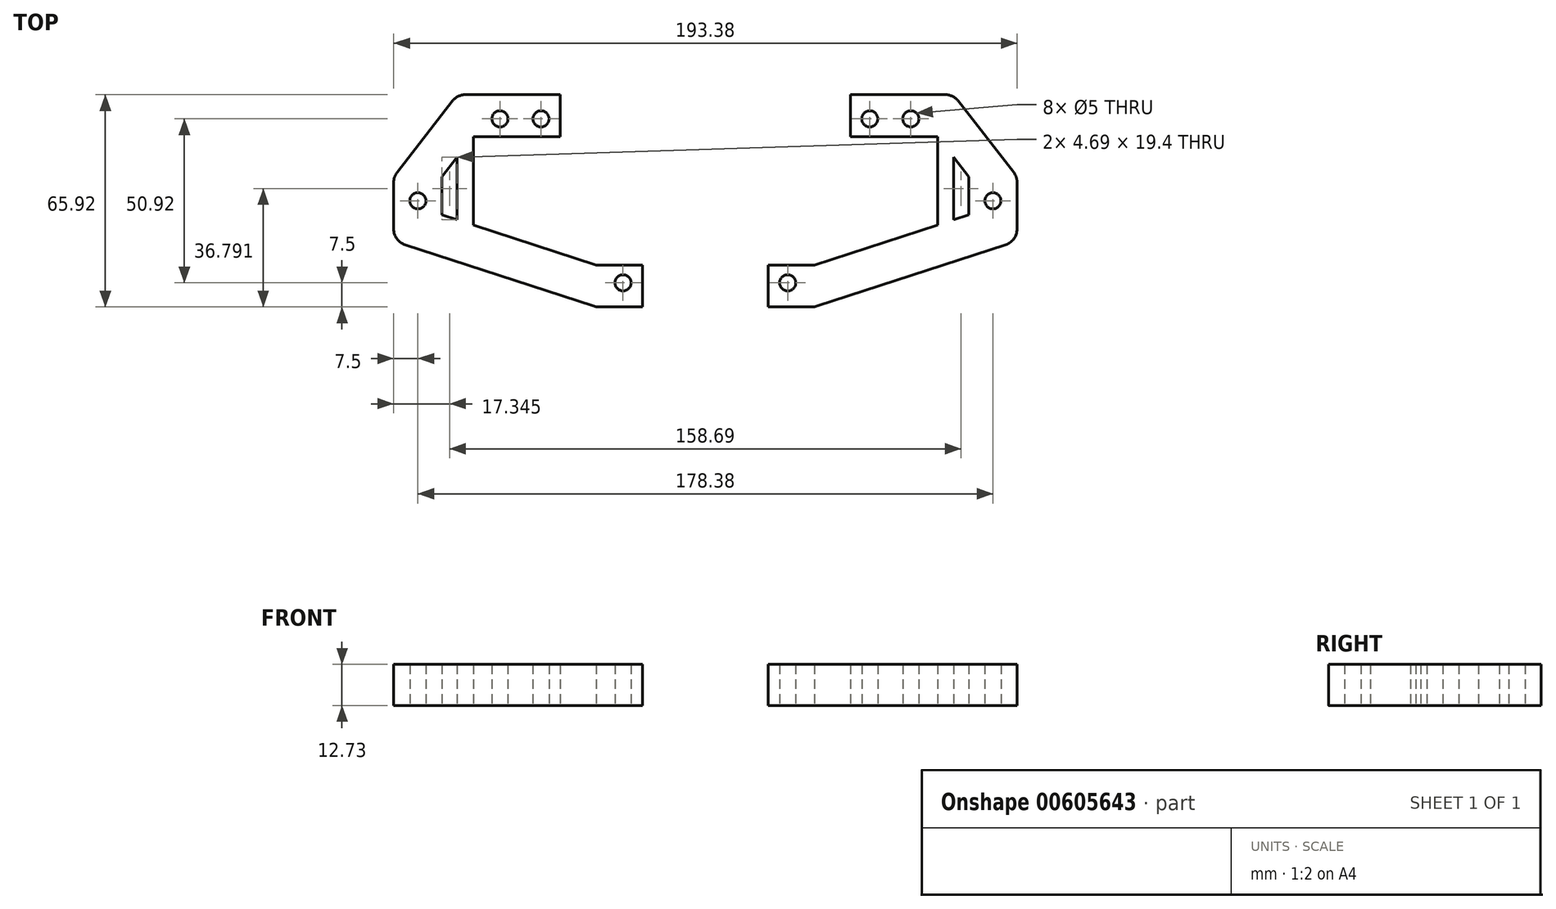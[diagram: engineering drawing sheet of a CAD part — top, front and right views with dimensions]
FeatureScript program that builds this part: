
annotation { "Feature Type Name" : "Feature", "Feature Type Description" : "" }
export const myFeature = defineFeature(function(context is Context, id is Id, definition is map)
    precondition{}
    {
        {
            var Q0;
            Q0=qCreatedBy(makeId("Top.planeOp"),FACE);
            var sketch = newSketch(context, id + "F0", { "sketchPlane" : qUnion([Q0])});
            skPoint(sketch, "E0", {"position": v(0, 0) * mm});
            skPoint(sketch, "E1", {"position": v(0, -50.92) * mm});
            skPoint(sketch, "E2", {"position": v(25.46, -50.92) * mm});
            skPoint(sketch, "E3", {"position": v(-12.73, 0) * mm});
            skPoint(sketch, "E4", {"position": v(0, -25.46) * mm});
            skPoint(sketch, "E5", {"position": v(-38.2, -25.46) * mm});
            skLineSegment(sketch, "E6.left", {"start": v(-45.7, -32.96) * mm, "end": v(-45.7, -17.96) * mm});
            skPoint(sketch, "E7.start.orphan", {"position": v(6, 0) * mm});
            skLineSegment(sketch, "E8", {"start": v(6, 5.5) * mm, "end": v(6, -5.5) * mm});
            skLineSegment(sketch, "E9", {"start": v(6, -5.5) * mm, "end": v(-21, -5.5) * mm});
            skLineSegment(sketch, "E10", {"start": v(31.46, -45.42) * mm, "end": v(17.2, -45.42) * mm});
            skLineSegment(sketch, "E11", {"start": v(-45.69, -17.96) * mm, "end": v(-27.45, 5.5) * mm});
            skLineSegment(sketch, "E12", {"start": v(-21, -5.5) * mm, "end": v(-21, -32.96) * mm});
            skLineSegment(sketch, "E13", {"start": v(-21, -32.96) * mm, "end": v(17.2, -45.42) * mm});
            skLineSegment(sketch, "E14", {"start": v(-45.7, -35.9) * mm, "end": v(-45.7, -32.96) * mm});
            skCircle(sketch, "E15", {"center": v(-12.73, 0) * mm, "radius": 2.5 * mm});
            skCircle(sketch, "E16", {"center": v(0, 0) * mm, "radius": 2.5 * mm});
            skCircle(sketch, "E17", {"center": v(-38.2, -25.46) * mm, "radius": 2.5 * mm});
            skCircle(sketch, "E18", {"center": v(25.46, -50.92) * mm, "radius": 2.5 * mm});
            skPoint(sketch, "E19", {"position": v(-30.7, -25.46) * mm});
            skLineSegment(sketch, "E20", {"start": v(-21, -32.96) * mm, "end": v(-30.7, -29.8) * mm});
            skLineSegment(sketch, "E21", {"start": v(-21, -5.5) * mm, "end": v(-30.7, -17.96) * mm});
            skLineSegment(sketch, "E22", {"start": v(-30.7, -17.96) * mm, "end": v(-30.7, -29.8) * mm});
            skPoint(sketch, "E23", {"position": v(-26, -25.46) * mm});
            skLineSegment(sketch, "E24", {"start": v(-26, -25.46) * mm, "end": v(-26, -11.93) * mm});
            skLineSegment(sketch, "E25", {"start": v(-26, -25.46) * mm, "end": v(-26, -31.33) * mm});
            skPoint(sketch, "E26", {"position": v(6, 7.5) * mm});
            skLineSegment(sketch, "E27", {"start": v(6, 7.5) * mm, "end": v(-25.9, 7.5) * mm});
            skLineSegment(sketch, "E28", {"start": v(-27.45, 5.5) * mm, "end": v(-25.9, 7.5) * mm});
            skLineSegment(sketch, "E29", {"start": v(6, 7.5) * mm, "end": v(6, 5.5) * mm});
            skLineSegment(sketch, "E30", {"start": v(17.2, -58.42) * mm, "end": v(-45.7, -37.9) * mm});
            skLineSegment(sketch, "E31", {"start": v(-45.7, -37.9) * mm, "end": v(-45.7, -35.9) * mm});
            skLineSegment(sketch, "E32", {"start": v(17.2, -58.42) * mm, "end": v(31.46, -58.42) * mm});
            skPoint(sketch, "E33", {"position": v(31.46, -50.92) * mm});
            skLineSegment(sketch, "E34", {"start": v(31.46, -45.42) * mm, "end": v(31.46, -58.42) * mm});
            skPoint(sketch, "E35", {"position": v(31.46, -45.42) * mm});
            skPoint(sketch, "E36", {"position": v(31.46, -58.42) * mm});
            skSolve(sketch);
        }
        {
            var Q0;
            Q0=makeQuery(id+"F0.imprint","IMPRINT",FACE,{"disambiguationData":[TD([[makeQuery(id+"F0.imprint","IMPRINT",EDGE,{"derivedFrom":sQuery(id+"F0.wireOp",EDGE,"E6.left")}),-1.0]])]});
            var Q1;
            {var subQ1=sQuery(id+"F0.wireOp",EDGE,"E12");Q1=makeQuery(id+"F0.imprint","IMPRINT",FACE,{"disambiguationData":[TD([[makeQuery(id+"F0.imprint","IMPRINT",EDGE,{"derivedFrom":subQ1}),-1.0]])]});}
            extrude(context, id + "F1", {"entities" : qUnion([Q0, Q1]), "depth" : 12.73 * mm, "offsetDistance" : 25 * mm});
        }
        {
            var Q0;
            Q0=makeQuery(id+"F1.opExtrude","SWEPT_EDGE",EDGE,{"disambiguationData":[OSD([sQuery(id+"F0.wireOp",EDGE,"E27"),sQuery(id+"F0.wireOp",EDGE,"E28")])]});
            var Q1;
            Q1=makeQuery(id+"F1.opExtrude","SWEPT_EDGE",EDGE,{"disambiguationData":[OSD([sQuery(id+"F0.wireOp",EDGE,"E6.left"),sQuery(id+"F0.wireOp",EDGE,"E11")])]});
            var Q2;
            Q2=makeQuery(id+"F1.opExtrude","SWEPT_EDGE",EDGE,{"disambiguationData":[OSD([sQuery(id+"F0.wireOp",EDGE,"E30"),sQuery(id+"F0.wireOp",EDGE,"E31")])]});
            var Q3;
            Q3=makeQuery(id+"F1.opExtrude","SWEPT_EDGE",EDGE,{"disambiguationData":[OSD([sQuery(id+"F0.wireOp",EDGE,"E30"),sQuery(id+"F0.wireOp",EDGE,"E32")])]});
            fillet(context, id + "F2", {"entities" : qUnion([Q0, Q1, Q2, Q3]), "radius" : 5 * mm, "tangentPropagation" : true, "allowEdgeOverflow" : false});
        }
        {
            var Q0;
            Q0=makeQuery(id+"F1.opExtrude","SWEPT_BODY",BODY,{"disambiguationData":[OSD([sQuery(id+"F0.wireOp",EDGE,"E6.left"),sQuery(id+"F0.wireOp",EDGE,"E8"),sQuery(id+"F0.wireOp",EDGE,"E9"),sQuery(id+"F0.wireOp",EDGE,"E10"),sQuery(id+"F0.wireOp",EDGE,"E11"),sQuery(id+"F0.wireOp",EDGE,"E12"),sQuery(id+"F0.wireOp",EDGE,"E13"),sQuery(id+"F0.wireOp",EDGE,"E14"),sQuery(id+"F0.wireOp",EDGE,"E15"),sQuery(id+"F0.wireOp",EDGE,"E16"),sQuery(id+"F0.wireOp",EDGE,"E17"),sQuery(id+"F0.wireOp",EDGE,"E18"),sQuery(id+"F0.wireOp",EDGE,"E20"),sQuery(id+"F0.wireOp",EDGE,"E21"),sQuery(id+"F0.wireOp",EDGE,"E22"),sQuery(id+"F0.wireOp",EDGE,"E24"),sQuery(id+"F0.wireOp",EDGE,"E25"),sQuery(id+"F0.wireOp",EDGE,"E27"),sQuery(id+"F0.wireOp",EDGE,"E28"),sQuery(id+"F0.wireOp",EDGE,"E29"),sQuery(id+"F0.wireOp",EDGE,"E30"),sQuery(id+"F0.wireOp",EDGE,"E31"),sQuery(id+"F0.wireOp",EDGE,"E32"),sQuery(id+"F0.wireOp",EDGE,"E34")])]});
            transform(context, id + "F3", {"entities" : qUnion([Q0]), "transformType" : TransformType.TRANSLATION_3D, "dx" : -51 * mm, "dy" : 0 * mm, "dz" : 0 * mm, "makeCopy" : false});
        }
        {
            var Q0;
            Q0=makeQuery(id+"F1.opExtrude","SWEPT_BODY",BODY,{"disambiguationData":[OSD([sQuery(id+"F0.wireOp",EDGE,"E6.left"),sQuery(id+"F0.wireOp",EDGE,"E8"),sQuery(id+"F0.wireOp",EDGE,"E9"),sQuery(id+"F0.wireOp",EDGE,"E10"),sQuery(id+"F0.wireOp",EDGE,"E11"),sQuery(id+"F0.wireOp",EDGE,"E12"),sQuery(id+"F0.wireOp",EDGE,"E13"),sQuery(id+"F0.wireOp",EDGE,"E14"),sQuery(id+"F0.wireOp",EDGE,"E15"),sQuery(id+"F0.wireOp",EDGE,"E16"),sQuery(id+"F0.wireOp",EDGE,"E17"),sQuery(id+"F0.wireOp",EDGE,"E18"),sQuery(id+"F0.wireOp",EDGE,"E20"),sQuery(id+"F0.wireOp",EDGE,"E21"),sQuery(id+"F0.wireOp",EDGE,"E22"),sQuery(id+"F0.wireOp",EDGE,"E24"),sQuery(id+"F0.wireOp",EDGE,"E25"),sQuery(id+"F0.wireOp",EDGE,"E27"),sQuery(id+"F0.wireOp",EDGE,"E28"),sQuery(id+"F0.wireOp",EDGE,"E29"),sQuery(id+"F0.wireOp",EDGE,"E30"),sQuery(id+"F0.wireOp",EDGE,"E31"),sQuery(id+"F0.wireOp",EDGE,"E32"),sQuery(id+"F0.wireOp",EDGE,"E34")])]});
            var Q1;
            Q1=qCreatedBy(makeId("Right.planeOp"),FACE);
            mirror(context, id + "F4", {"entities" : qUnion([Q0]), "mirrorPlane" : qUnion([Q1])});
        }
    });
